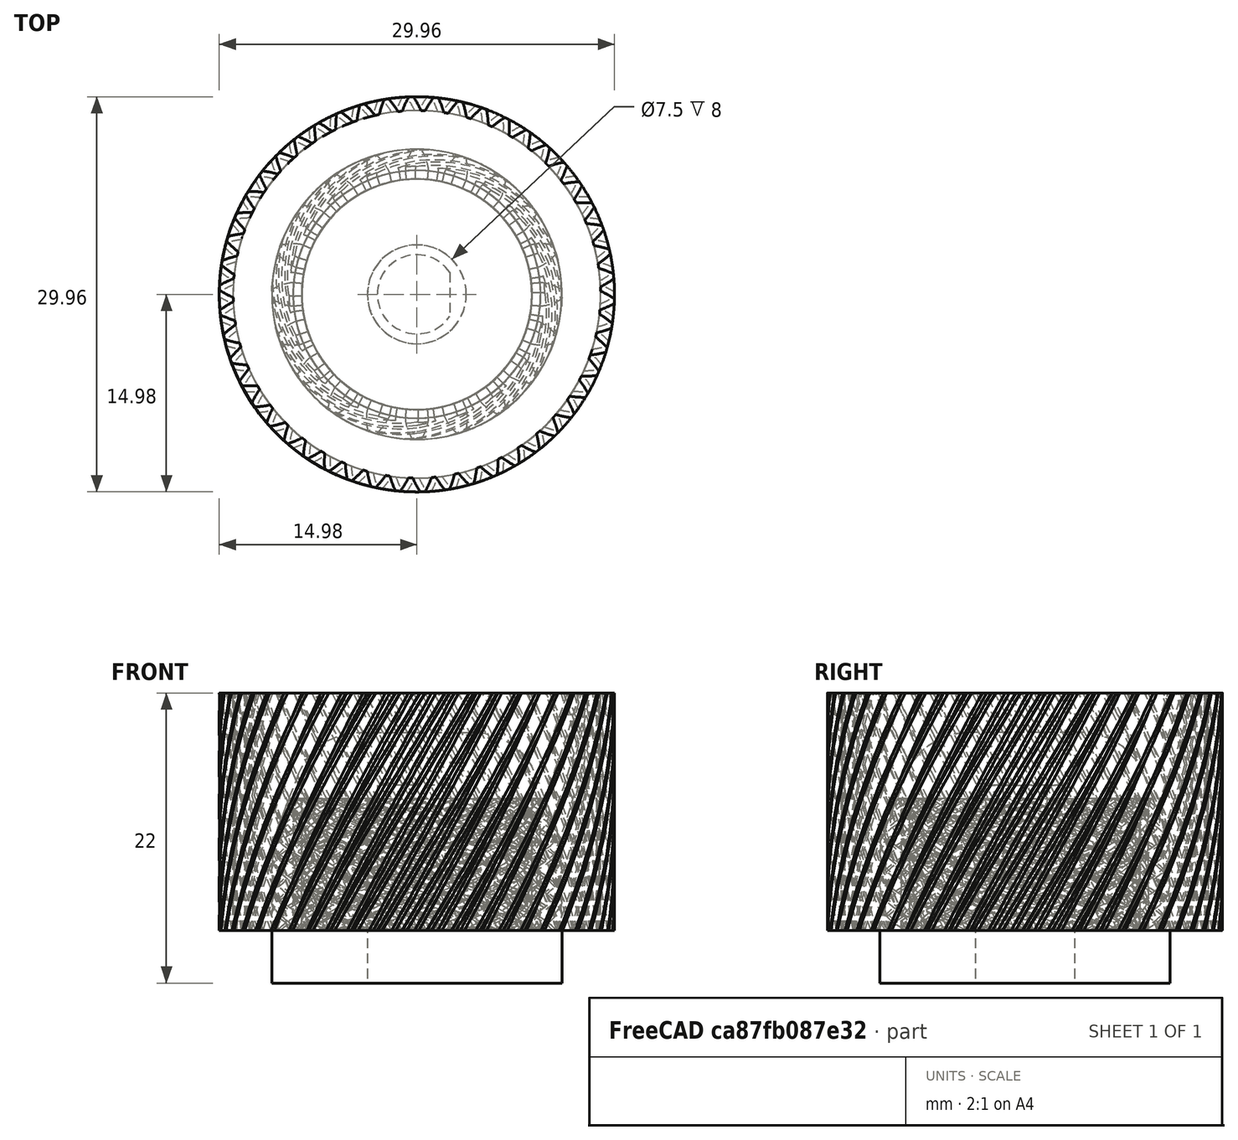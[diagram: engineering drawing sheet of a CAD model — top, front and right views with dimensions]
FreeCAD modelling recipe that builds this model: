
FCSTD DOCUMENT  (FreeCAD 0.20R29410 (Git))
Label: controller
License: Creative Commons Attribution
LicenseURL: http://creativecommons.org/licenses/by/4.0/
objects: Sketcher::SketchObject×6, PartDesign::Pad×3, PartDesign::FeaturePython×2, PartDesign::Body×2, PartDesign::Pocket×2, PartDesign::Groove×1, PartDesign::Fillet×1, App::Part×1, Mesh::Feature×1
note: 24 computed .brp shape members not serialized (recipe doc carries the construction recipe); baked Part::Feature solids carry a one-line shape summary decoded from their .brp

FEATURE [PartDesign::FeaturePython] involutegear  # WARN: FeaturePython — macro-defined, semantics opaque (R4)
  AttacherType = Attacher::AttachEngine3D
  backlash = 0
  beta = 30
  clearance = 0.1
  da = 29.9675
  df = 27.8675
  double_helix = false
  dw = 28.8675
  head = 0
  height = 18
  module = 0.5
  numpoints = 6
  pressure_angle = 25
  properties_from_tool = true
  reversed_backlash = false
  shift = 0.1
  simple = false
  teeth = 50
  transverse_pitch = 1.8138
  undercut = false
  version = 0.0.3
FEATURE [PartDesign::Body] Body  label="Knob"
  Group = -> [involutegear]
  Origin = -> Origin001
  Tip = -> involutegear
FEATURE [PartDesign::FeaturePython] involutegear001  # WARN: FeaturePython — macro-defined, semantics opaque (R4)
  AttacherType = Attacher::AttachEngine3D
  backlash = 0
  beta = 70
  clearance = 0.25
  da = 22
  df = 17.5
  double_helix = false
  dw = 20
  head = 0
  height = 10
  module = 1
  numpoints = 6
  pressure_angle = 20
  properties_from_tool = false
  reversed_backlash = false
  shift = 0
  simple = false
  teeth = 20
  transverse_pitch = 3.14159
  undercut = false
  version = 0.0.3
FEATURE [Sketcher::SketchObject] Sketch
  FullyConstrained = true
  MapMode = 5
  Placement = pos=(-0.000158241,6.58077e-05,10.0002) rot=(-0.383989,-0.923338,3e-06;1.7e-05rad)
  Support = -> [involutegear001]
  sketch-geometry (1):
    g0: Circle CenterX=0 CenterY=0 CenterZ=0 NormalX=0 NormalY=0 NormalZ=1 AngleXU=0 Radius=10
  constraints (2):
    c: Coincident(g0,g-1)
    c: Diameter(g0) = 20
FEATURE [PartDesign::Pad] Pad
  BaseFeature = -> involutegear001
  Direction = (-1.58238e-05,6.58066e-06,1)
  Length = 5
  Length2 = 10
  Profile = -> Sketch
  ReferenceAxis = -> Sketch [N_Axis]
  Type = 0
FEATURE [Sketcher::SketchObject] Sketch001
  FullyConstrained = false
  MapMode = 5
  Placement = pos=(0,0,0) rot=(0.57735,0.57735,0.57735;2.0944rad)
  Support = -> [YZ_Plane002]
  sketch-geometry (3):
    g0: LineSegment StartX=-7.41297 StartY=15.8482 StartZ=0 EndX=-11.5507 EndY=5.25851 EndZ=0
    g1: LineSegment StartX=-11.5507 StartY=5.25851 StartZ=0 EndX=-17.7572 EndY=13.569 EndZ=0
    g2: LineSegment StartX=-17.7572 StartY=13.569 StartZ=0 EndX=-7.41297 EndY=15.8482 EndZ=0
  constraints (3):
    c: Coincident(g0,g1)
    c: Coincident(g1,g2)
    c: Coincident(g2,g0)
FEATURE [PartDesign::Groove] Groove
  Angle = 360
  Axis = (-2e-16,3e-16,1)
  Base = (0,0,0)
  BaseFeature = -> Pad
  Profile = -> Sketch001
  ReferenceAxis = -> Sketch001 [V_Axis]
  Reversed = true
FEATURE [Sketcher::SketchObject] Sketch002
  ExternalGeometry = -> [Groove]
  FullyConstrained = true
  MapMode = 5
  Placement = pos=(0,0,0) rot=(1,0,0;3.14159rad)
  Support = -> [Groove]
  sketch-geometry (1):
    g0: Circle CenterX=0 CenterY=0 CenterZ=0 NormalX=0 NormalY=0 NormalZ=1 AngleXU=0 Radius=11
  constraints (2):
    c: Coincident(g0,g-1)
    c: Diameter(g0) = 22
FEATURE [PartDesign::Pad] Pad001
  BaseFeature = -> Groove
  Direction = (0,0,-1)
  Length = 4
  Length2 = 10
  Profile = -> Sketch002
  ReferenceAxis = -> Sketch002 [N_Axis]
  Type = 0
FEATURE [Sketcher::SketchObject] Sketch003
  FullyConstrained = true
  MapMode = 5
  Placement = pos=(0,-1e-16,-4) rot=(1,0,0;3.14159rad)
  Support = -> [Pad001]
  sketch-geometry (1):
    g0: Circle CenterX=0 CenterY=0 CenterZ=0 NormalX=0 NormalY=0 NormalZ=1 AngleXU=0 Radius=3
  constraints (2):
    c: Coincident(g0,g-1)
    c: Diameter(g0) = 6
FEATURE [PartDesign::Pocket] Pocket
  BaseFeature = -> Pad001
  Direction = (0,0,1)
  Length = 15
  Length2 = 5
  Profile = -> Sketch003
  ReferenceAxis = -> Sketch003 [N_Axis]
  Type = 0
FEATURE [Sketcher::SketchObject] Sketch004
  FullyConstrained = true
  MapMode = 5
  Placement = pos=(0,-1e-16,-4) rot=(1,0,0;3.14159rad)
  Support = -> [Pocket]
  sketch-geometry (1):
    g0: Circle CenterX=0 CenterY=0 CenterZ=0 NormalX=0 NormalY=0 NormalZ=1 AngleXU=0 Radius=3.75
  constraints (2):
    c: Coincident(g0,g-1)
    c: Diameter(g0) = 7.5
FEATURE [PartDesign::Pocket] Pocket001
  BaseFeature = -> Pocket
  Direction = (0,0,1)
  Length = 8
  Length2 = 5
  Profile = -> Sketch004
  ReferenceAxis = -> Sketch004 [N_Axis]
  Type = 0
FEATURE [Sketcher::SketchObject] Sketch005
  FullyConstrained = false
  MapMode = 5
  Placement = pos=(0,0,4) rot=(1,0,0;3.14159rad)
  Support = -> [Pocket001]
  expr: Constraints[8] = 5 / 2
  sketch-geometry (4):
    g0: LineSegment StartX=2.5 StartY=2.6254 StartZ=0 EndX=4.40379 EndY=2.6254 EndZ=0
    g1: LineSegment StartX=4.40379 StartY=2.6254 StartZ=0 EndX=4.40379 EndY=-2.9149 EndZ=0
    g2: LineSegment StartX=4.40379 StartY=-2.9149 StartZ=0 EndX=2.5 EndY=-2.9149 EndZ=0
    g3: LineSegment StartX=2.5 StartY=-2.9149 StartZ=0 EndX=2.5 EndY=2.6254 EndZ=0
  constraints (9):
    c: Coincident(g0,g1)
    c: Coincident(g1,g2)
    c: Coincident(g2,g3)
    c: Coincident(g3,g0)
    c: Horizontal(g0)
    c: Horizontal(g2)
    c: Vertical(g1)
    c: Vertical(g3)
    c: DistanceX(g-1,g0) = 2.5
FEATURE [PartDesign::Pad] Pad002
  BaseFeature = -> Pocket001
  Direction = (0,0,-1)
  Length = 10
  Length2 = 10
  Profile = -> Sketch005
  ReferenceAxis = -> Sketch005 [N_Axis]
  Type = 3
  UpToFace = -> Pocket001 [Face191]
FEATURE [PartDesign::Fillet] Fillet
  Base = -> Pad002 [Edge456]
  BaseFeature = -> Pad002
  Radius = 5
  SupportTransform = false
  UseAllEdges = false
FEATURE [PartDesign::Body] Body001
  Group = -> [involutegear001,Sketch,Pad,Sketch001,Groove,Sketch002,Pad001,Sketch003,Pocket,Sketch004,Pocket001,Sketch005,Pad002,Fillet]
  Origin = -> Origin002
  Tip = -> Fillet
FEATURE [App::Part] Part
  Group = -> [Body,Body001]
  Origin = -> Origin
FEATURE [Mesh::Feature] Mesh  label="Body001 (Meshed)"
